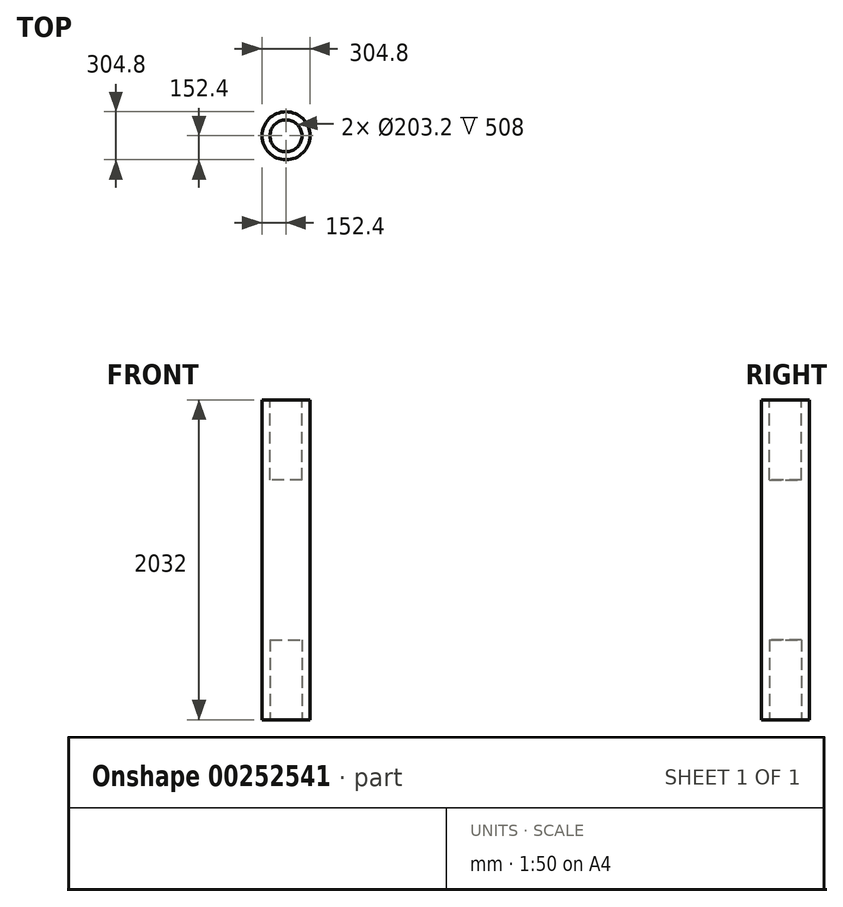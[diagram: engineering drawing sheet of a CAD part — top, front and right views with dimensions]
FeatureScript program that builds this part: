
annotation { "Feature Type Name" : "Feature", "Feature Type Description" : "" }
export const myFeature = defineFeature(function(context is Context, id is Id, definition is map)
    precondition{}
    {
        {
            var Q0;
            Q0=qCreatedBy(makeId("Top.planeOp"),FACE);
            var sketch = newSketch(context, id + "F0", { "sketchPlane" : qUnion([Q0])});
            skCircle(sketch, "E0", {"center": v(0, 0) * mm, "radius": 152.4 * mm});
            skSolve(sketch);
        }
        {
            var Q0;
            Q0=makeQuery(id+"F0.imprint","IMPRINT",FACE,{"disambiguationData":[TD([[makeQuery(id+"F0.imprint","IMPRINT",EDGE,{"derivedFrom":sQuery(id+"F0.wireOp",EDGE,"E0")}),1.0]])]});
            extrude(context, id + "F1", {"entities" : qUnion([Q0]), "depth" : 2032 * mm});
        }
        {
            var Q0;
            Q0=makeQuery(id+"F1.opExtrude","CAP_FACE",FACE,{"disambiguationData":[OSD([sQuery(id+"F0.wireOp",EDGE,"E0")])],"isStart":true});
            var sketch = newSketch(context, id + "F2", { "sketchPlane" : qUnion([Q0])});
            skCircle(sketch, "E1", {"center": v(0, 0) * mm, "radius": 101.6 * mm});
            skSolve(sketch);
        }
        {
            var Q0;
            Q0=makeQuery(id+"F2.imprint","IMPRINT",FACE,{"disambiguationData":[TD([[makeQuery(id+"F2.imprint","IMPRINT",EDGE,{"derivedFrom":sQuery(id+"F2.wireOp",EDGE,"E1")}),1.0]])]});
            extrude(context, id + "F3", {"entities" : qUnion([Q0]), "operationType" : NewBodyOperationType.REMOVE, "oppositeDirection" : true, "depth" : 508 * mm});
        }
        {
            var Q0;
            Q0=makeQuery(id+"F1.opExtrude","CAP_FACE",FACE,{"disambiguationData":[OSD([sQuery(id+"F0.wireOp",EDGE,"E0")])],"isStart":false});
            var sketch = newSketch(context, id + "F4", { "sketchPlane" : qUnion([Q0])});
            skCircle(sketch, "E2", {"center": v(0, 0) * mm, "radius": 101.6 * mm});
            skSolve(sketch);
        }
        {
            var Q0;
            Q0=makeQuery(id+"F4.imprint","IMPRINT",FACE,{"disambiguationData":[TD([[makeQuery(id+"F4.imprint","IMPRINT",EDGE,{"derivedFrom":sQuery(id+"F4.wireOp",EDGE,"E2")}),1.0]])]});
            extrude(context, id + "F5", {"entities" : qUnion([Q0]), "operationType" : NewBodyOperationType.REMOVE, "oppositeDirection" : true, "depth" : 508 * mm});
        }
    });
